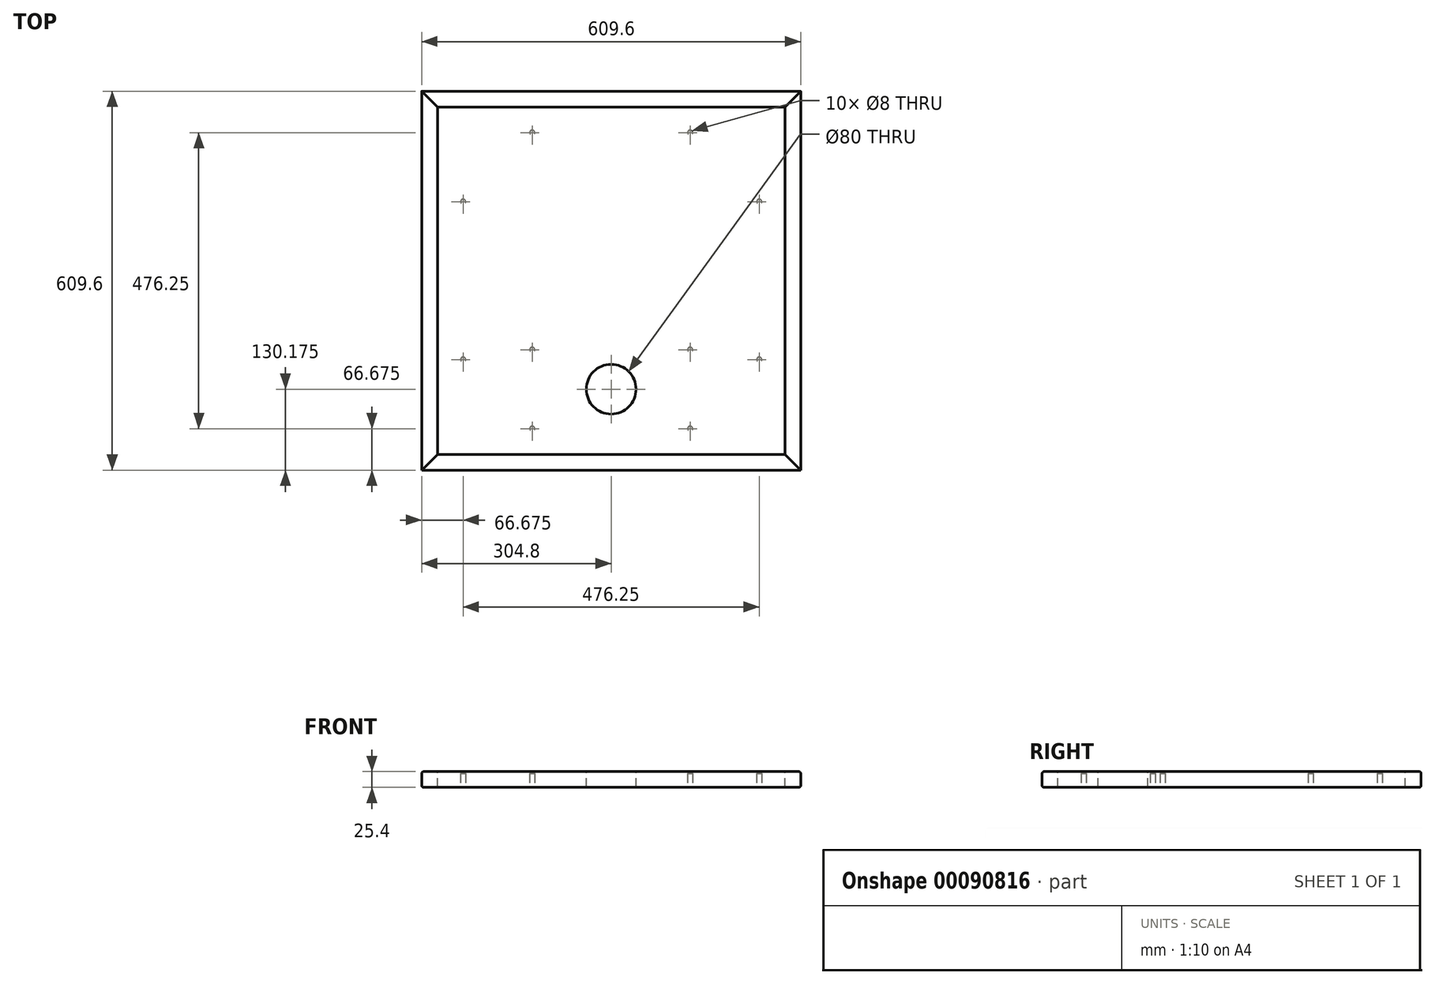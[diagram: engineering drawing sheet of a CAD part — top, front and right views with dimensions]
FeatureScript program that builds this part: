
annotation { "Feature Type Name" : "Feature", "Feature Type Description" : "" }
export const myFeature = defineFeature(function(context is Context, id is Id, definition is map)
    precondition{}
    {
        {
            var Q0;
            Q0=qCreatedBy(makeId("Top.planeOp"),FACE);
            var sketch = newSketch(context, id + "F0", { "sketchPlane" : qUnion([Q0])});
            skLineSegment(sketch, "E0.bottom", {"start": v(279.4, -279.4) * mm, "end": v(-279.4, -279.4) * mm});
            skLineSegment(sketch, "E0.top", {"start": v(279.4, 279.4) * mm, "end": v(-279.4, 279.4) * mm});
            skLineSegment(sketch, "E0.left", {"start": v(279.4, -279.4) * mm, "end": v(279.4, 279.4) * mm});
            skLineSegment(sketch, "E0.right", {"start": v(-279.4, -279.4) * mm, "end": v(-279.4, 279.4) * mm});
            skPoint(sketch, "E0.middle", {"position": v(0, 0) * mm});
            skSolve(sketch);
        }
        {
            var Q0;
            Q0=makeQuery(id+"F0.imprint","IMPRINT",FACE,{"disambiguationData":[TD([[makeQuery(id+"F0.imprint","IMPRINT",EDGE,{"derivedFrom":sQuery(id+"F0.wireOp",EDGE,"E0.bottom")}),-1.0]])]});
            extrude(context, id + "F1", {"entities" : qUnion([Q0]), "depth" : 25.4 * mm});
        }
        {
            var Q0;
            Q0=makeQuery(id+"F1.opExtrude","CAP_FACE",FACE,{"disambiguationData":[OSD([sQuery(id+"F0.wireOp",EDGE,"E0.bottom"),sQuery(id+"F0.wireOp",EDGE,"E0.top"),sQuery(id+"F0.wireOp",EDGE,"E0.left"),sQuery(id+"F0.wireOp",EDGE,"E0.right")])],"isStart":true});
            var sketch = newSketch(context, id + "F2", { "sketchPlane" : qUnion([Q0])});
            skLineSegment(sketch, "E1", {"start": v(0, 279.4) * mm, "end": v(0, -279.4) * mm, "construction": true});
            skPoint(sketch, "E2", {"position": v(-127, 238.13) * mm});
            skPoint(sketch, "E3", {"position": v(-127, 111.13) * mm});
            skPoint(sketch, "E4", {"position": v(-238.13, 127) * mm});
            skPoint(sketch, "E5", {"position": v(-238.13, -127) * mm});
            skPoint(sketch, "E6", {"position": v(-127, -238.12) * mm});
            skPoint(sketch, "E7.MirrorP", {"position": v(127, 238.13) * mm});
            skPoint(sketch, "E8.MirrorP", {"position": v(127, 111.13) * mm});
            skPoint(sketch, "E9.MirrorP", {"position": v(238.12, 127) * mm});
            skPoint(sketch, "E10.MirrorP", {"position": v(238.13, -127) * mm});
            skPoint(sketch, "E11.MirrorP", {"position": v(127, -238.12) * mm});
            skSolve(sketch);
        }
        {
            var Q0;
            Q0=sQuery(id+"F2.wireOp",VERTEX,"E7.MirrorP");
            var Q1;
            Q1=sQuery(id+"F2.wireOp",VERTEX,"E8.MirrorP");
            var Q2;
            Q2=sQuery(id+"F2.wireOp",VERTEX,"E9.MirrorP");
            var Q3;
            Q3=sQuery(id+"F2.wireOp",VERTEX,"E10.MirrorP");
            var Q4;
            Q4=sQuery(id+"F2.wireOp",VERTEX,"E11.MirrorP");
            var Q5;
            Q5=sQuery(id+"F2.wireOp",VERTEX,"E6");
            var Q6;
            Q6=sQuery(id+"F2.wireOp",VERTEX,"E5");
            var Q7;
            Q7=sQuery(id+"F2.wireOp",VERTEX,"E4");
            var Q8;
            Q8=sQuery(id+"F2.wireOp",VERTEX,"E3");
            var Q9;
            Q9=sQuery(id+"F2.wireOp",VERTEX,"E2");
            var Q10;
            Q10=makeQuery(id+"F1.opExtrude","SWEPT_BODY",BODY,{"disambiguationData":[OSD([sQuery(id+"F0.wireOp",EDGE,"E0.bottom"),sQuery(id+"F0.wireOp",EDGE,"E0.top"),sQuery(id+"F0.wireOp",EDGE,"E0.left"),sQuery(id+"F0.wireOp",EDGE,"E0.right")])]});
            hole(context, id + "F3", {"style" : HoleStyle.SIMPLE, "endStyle" : HoleEndStyle.BLIND, "holeDiameter" : 8 * mm, "holeDepth" : 22.22 * mm, "startFromSketch" : true, "locations" : qUnion([Q0, Q1, Q2, Q3, Q4, Q5, Q6, Q7, Q8, Q9]), "scope" : qUnion([Q10])});
        }
        {
            var Q0;
            Q0=makeQuery(id+"F1.opExtrude","CAP_FACE",FACE,{"disambiguationData":[OSD([sQuery(id+"F0.wireOp",EDGE,"E0.bottom"),sQuery(id+"F0.wireOp",EDGE,"E0.top"),sQuery(id+"F0.wireOp",EDGE,"E0.left"),sQuery(id+"F0.wireOp",EDGE,"E0.right")])],"isStart":false});
            var sketch = newSketch(context, id + "F4", { "sketchPlane" : qUnion([Q0])});
            skCircle(sketch, "E12", {"center": v(0, -174.63) * mm, "radius": 40 * mm});
            skSolve(sketch);
        }
        {
            var Q0;
            Q0=makeQuery(id+"F4.imprint","IMPRINT",FACE,{"disambiguationData":[TD([[makeQuery(id+"F4.imprint","IMPRINT",EDGE,{"derivedFrom":sQuery(id+"F4.wireOp",EDGE,"E12")}),1.0]])]});
            extrude(context, id + "F5", {"entities" : qUnion([Q0]), "operationType" : NewBodyOperationType.REMOVE, "endBound" : BoundingType.THROUGH_ALL, "oppositeDirection" : true, "depth" : 25.4 * mm});
        }
        {
            var Q0;
            Q0=makeQuery(id+"F1.opExtrude","CAP_FACE",FACE,{"disambiguationData":[OSD([sQuery(id+"F0.wireOp",EDGE,"E0.bottom"),sQuery(id+"F0.wireOp",EDGE,"E0.top"),sQuery(id+"F0.wireOp",EDGE,"E0.left"),sQuery(id+"F0.wireOp",EDGE,"E0.right")])],"isStart":false});
            var sketch = newSketch(context, id + "F6", { "sketchPlane" : qUnion([Q0])});
            skLineSegment(sketch, "E13.0", {"start": v(279.4, -279.4) * mm, "end": v(279.4, 279.4) * mm});
            skLineSegment(sketch, "E14.0", {"start": v(304.8, -304.8) * mm, "end": v(304.8, 304.8) * mm});
            skLineSegment(sketch, "E15", {"start": v(279.4, 279.4) * mm, "end": v(304.8, 304.8) * mm});
            skLineSegment(sketch, "E16", {"start": v(279.4, -279.4) * mm, "end": v(304.8, -304.8) * mm});
            skSolve(sketch);
        }
        {
            var Q0;
            Q0=makeQuery(id+"F6.imprint","IMPRINT",FACE,{"disambiguationData":[TD([[makeQuery(id+"F6.imprint","IMPRINT",EDGE,{"derivedFrom":sQuery(id+"F6.wireOp",EDGE,"E13.0")}),-1.0]])]});
            extrude(context, id + "F7", {"entities" : qUnion([Q0]), "oppositeDirection" : true, "depth" : 25.4 * mm});
        }
        {
            var Q0;
            Q0=makeQuery(id+"F7.opExtrude","CAP_EDGE",EDGE,{"disambiguationData":[OSD([sQuery(id+"F6.wireOp",EDGE,"E14.0")])],"isStart":true});
            var Q1;
            Q1=makeQuery(id+"F7.opExtrude","CAP_EDGE",EDGE,{"disambiguationData":[OSD([sQuery(id+"F6.wireOp",EDGE,"E14.0")])],"isStart":false});
            fillet(context, id + "F8", {"entities" : qUnion([Q0, Q1]), "radius" : 3.17 * mm, "tangentPropagation" : true, "allowEdgeOverflow" : false});
        }
        {
            var Q0;
            Q0=makeQuery(id+"F7.opExtrude","SWEPT_BODY",BODY,{"disambiguationData":[OSD([sQuery(id+"F6.wireOp",EDGE,"E13.0"),sQuery(id+"F6.wireOp",EDGE,"E14.0"),sQuery(id+"F6.wireOp",EDGE,"E15"),sQuery(id+"F6.wireOp",EDGE,"E16")])]});
            var Q1;
            Q1=qCreatedBy(makeId("Right.planeOp"),FACE);
            mirror(context, id + "F9", {"entities" : qUnion([Q0]), "mirrorPlane" : qUnion([Q1])});
        }
        {
            var Q0;
            Q0=makeQuery(id+"F7.opExtrude","SWEPT_BODY",BODY,{"disambiguationData":[OSD([sQuery(id+"F6.wireOp",EDGE,"E13.0"),sQuery(id+"F6.wireOp",EDGE,"E14.0"),sQuery(id+"F6.wireOp",EDGE,"E15"),sQuery(id+"F6.wireOp",EDGE,"E16")])]});
            var Q1;
            Q1=makeQuery(id+"F7.opExtrude","SWEPT_EDGE",EDGE,{"disambiguationData":[OSD([sQuery(id+"F6.wireOp",EDGE,"E14.0"),sQuery(id+"F6.wireOp",EDGE,"E16")])]});
            transform(context, id + "F10", {"entities" : qUnion([Q0]), "transformType" : TransformType.ROTATION, "transformAxis" : qUnion([Q1]), "angle" : 90 * degree, "oppositeDirection" : true, "makeCopy" : true});
        }
        {
            var Q0;
            Q0=makeQuery(id+"F10.opPattern","COPY",BODY,{"derivedFrom":makeQuery(id+"F7.opExtrude","SWEPT_BODY",BODY,{"disambiguationData":[OSD([sQuery(id+"F6.wireOp",EDGE,"E13.0"),sQuery(id+"F6.wireOp",EDGE,"E14.0"),sQuery(id+"F6.wireOp",EDGE,"E15"),sQuery(id+"F6.wireOp",EDGE,"E16")])]}),"instanceName":"1"});
            var Q1;
            Q1=makeQuery(id+"F1.opExtrude","CAP_EDGE",EDGE,{"disambiguationData":[OSD([sQuery(id+"F0.wireOp",EDGE,"E0.bottom")])],"isStart":false});
            transform(context, id + "F11", {"entities" : qUnion([Q0]), "transformType" : TransformType.TRANSLATION_DISTANCE, "transformDirection" : qUnion([Q1]), "distance" : 609.6 * mm, "makeCopy" : false});
        }
        {
            var Q0;
            Q0=makeQuery(id+"F10.opPattern","COPY",BODY,{"derivedFrom":makeQuery(id+"F7.opExtrude","SWEPT_BODY",BODY,{"disambiguationData":[OSD([sQuery(id+"F6.wireOp",EDGE,"E13.0"),sQuery(id+"F6.wireOp",EDGE,"E14.0"),sQuery(id+"F6.wireOp",EDGE,"E15"),sQuery(id+"F6.wireOp",EDGE,"E16")])]}),"instanceName":"1"});
            var Q1;
            Q1=qCreatedBy(makeId("Front.planeOp"),FACE);
            mirror(context, id + "F12", {"entities" : qUnion([Q0]), "mirrorPlane" : qUnion([Q1])});
        }
    });
